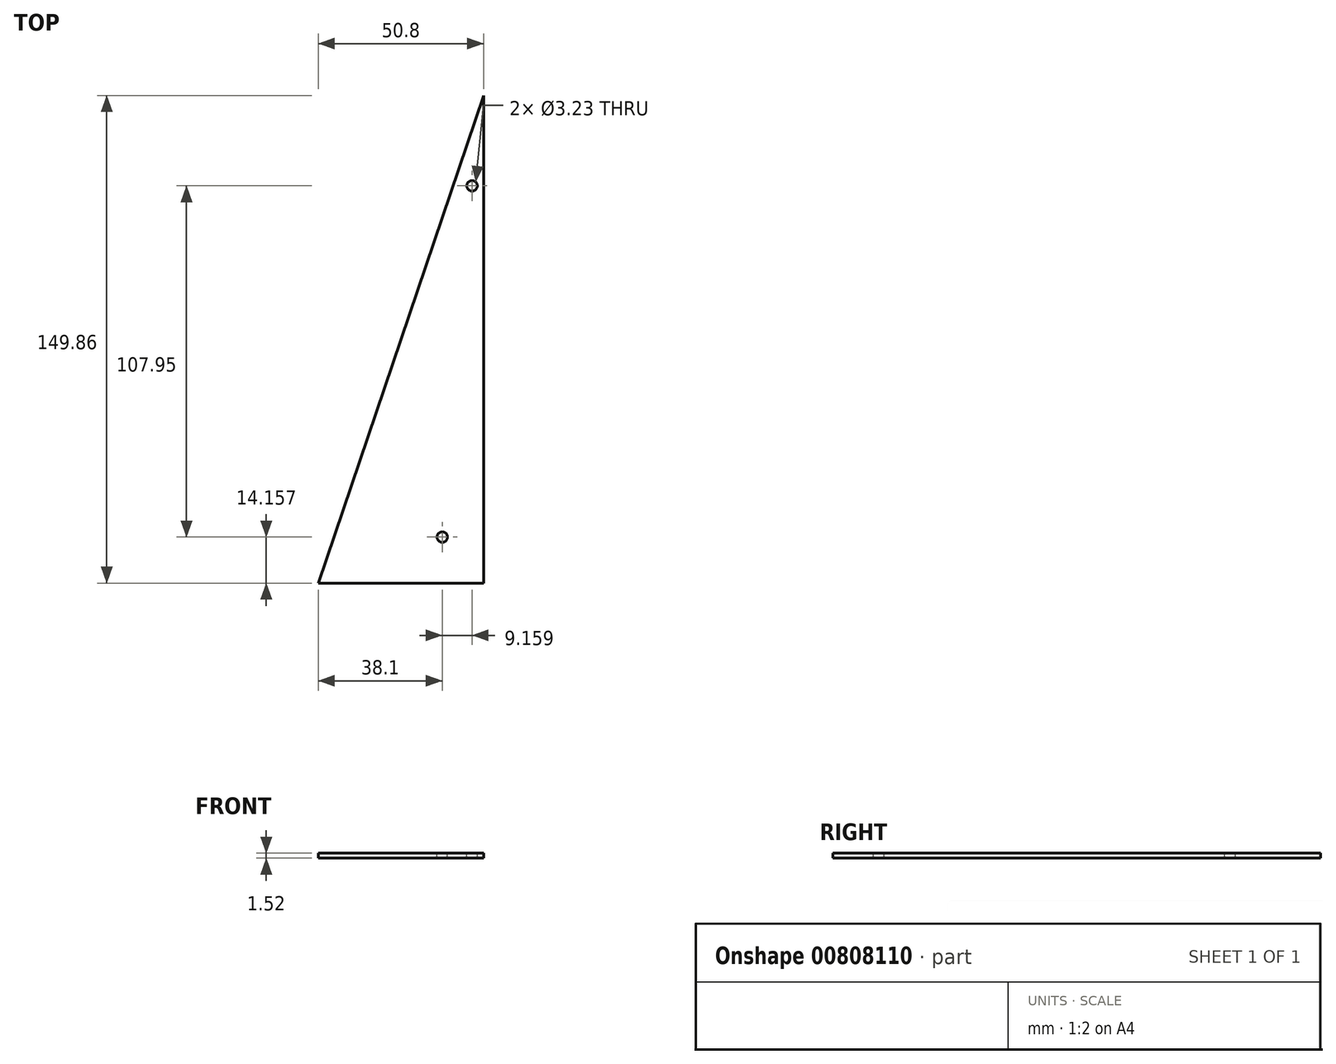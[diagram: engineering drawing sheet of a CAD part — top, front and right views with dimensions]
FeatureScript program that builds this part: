
annotation { "Feature Type Name" : "Feature", "Feature Type Description" : "" }
export const myFeature = defineFeature(function(context is Context, id is Id, definition is map)
    precondition{}
    {
        {
            var Q0;
            Q0=qCreatedBy(makeId("Top.planeOp"),FACE);
            var sketch = newSketch(context, id + "F0", { "sketchPlane" : qUnion([Q0])});
            skLineSegment(sketch, "E0.top", {"start": v(25.4, -74.93) * mm, "end": v(-25.4, -74.93) * mm});
            skLineSegment(sketch, "E0.left", {"start": v(25.4, 74.93) * mm, "end": v(25.4, -74.93) * mm});
            skPoint(sketch, "E0.middle", {"position": v(0, 0) * mm});
            skLineSegment(sketch, "E1", {"start": v(-25.4, -74.93) * mm, "end": v(25.4, 74.93) * mm});
            skPoint(sketch, "E0.bottom.end.orphan", {"position": v(-25.4, 74.93) * mm});
            skSolve(sketch);
        }
        {
            var Q0;
            Q0=qSketchRegion(id+"F0",true);
            extrude(context, id + "F1", {"entities" : qUnion([Q0]), "depth" : 1.52 * mm, "offsetDistance" : 25.4 * mm});
        }
        {
            var Q0;
            Q0=makeQuery(id+"F1.opExtrude","CAP_FACE",FACE,{"disambiguationData":[OSD([sQuery(id+"F0.wireOp",EDGE,"E0.bottom"),sQuery(id+"F0.wireOp",EDGE,"E0.top"),sQuery(id+"F0.wireOp",EDGE,"E0.left"),sQuery(id+"F0.wireOp",EDGE,"E0.right")])],"isStart":false});
            var sketch = newSketch(context, id + "F2", { "sketchPlane" : qUnion([Q0])});
            skCircle(sketch, "E2", {"center": v(21.86, 47.18) * mm, "radius": 1.61 * mm});
            skCircle(sketch, "E3", {"center": v(12.7, -60.77) * mm, "radius": 1.61 * mm});
            skLineSegment(sketch, "E4", {"start": v(12.7, -60.77) * mm, "end": v(25.4, -60.77) * mm});
            skSolve(sketch);
        }
        {
            var Q0;
            Q0=qSketchRegion(id+"F2",true);
            extrude(context, id + "F3", {"entities" : qUnion([Q0]), "operationType" : NewBodyOperationType.REMOVE, "oppositeDirection" : true, "depth" : 25.4 * mm, "offsetDistance" : 25.4 * mm});
        }
        {
            var Q0;
            Q0=qSketchRegion(id+"F2",true);
            extrude(context, id + "F4", {"entities" : qUnion([Q0]), "operationType" : NewBodyOperationType.REMOVE, "depth" : 39.37 * mm, "offsetDistance" : 25.4 * mm});
        }
    });
